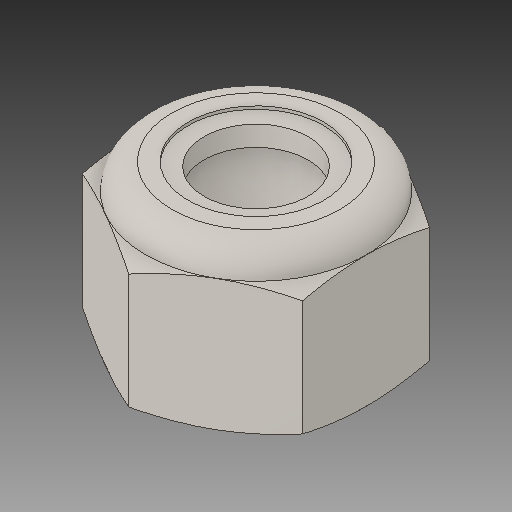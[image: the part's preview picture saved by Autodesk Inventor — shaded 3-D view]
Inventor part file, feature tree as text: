
AUTODESK INVENTOR PART (.ipt)
format: ipt  version: 2018 (Build 220112000, 112)  size: 192,000 bytes
history: native  units: in
note: dims shown in document units (in); Inventor stores cm internally (conversion verified against a paired STEP export)
features: other x1, revolve x1
ambient origin geometry x8: Origin, YZ Plane, XZ Plane, XY Plane, X Axis, Y Axis, Z Axis, Center Point
bodies: Solid1 (feature_tree), Solid2 (feature_tree)
feature tree (2):
  other  "Cut-Revolve2"
  revolve  "Revolve1"  [1 undecoded]
note: 1 required parameter value undecoded (feature->parameter linkage not recoverable at this tier; creation-order binding heuristic only, values carry confidence <= 0.55)
